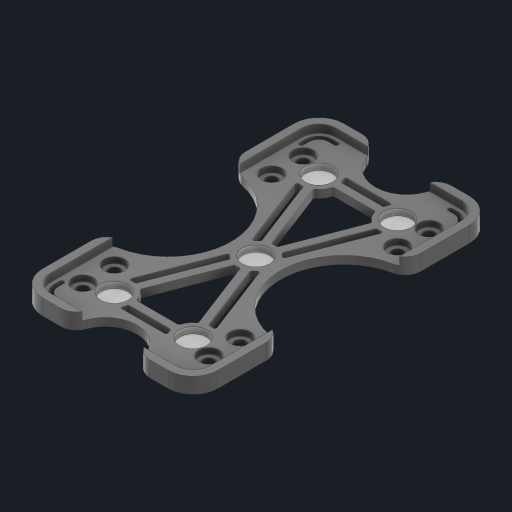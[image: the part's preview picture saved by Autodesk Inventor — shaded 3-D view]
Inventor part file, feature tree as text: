
AUTODESK INVENTOR PART (.ipt)
format: ipt  version: 2024 (Build 280153000, 153)  size: 400,896 bytes
history: native  units: in
note: dims shown in document units (in); Inventor stores cm internally (conversion verified against a paired STEP export)
features: extrude x1, sketch x1
ambient origin geometry x8: Origin, YZ Plane, XZ Plane, XY Plane, X Axis, Y Axis, Z Axis, Center Point
bodies: Solid2 (feature_tree), Solid1 (feature_tree)
feature tree (2):
  extrude  "Extrusion1"  Depth=0.0984in
  sketch  "Sketch1"  dims[d0=0.4331in d1=0.4331in d2=0.4331in d3=0.4331in d4=0.4331in d5=0.0984in d6=0.0in]
